# Revit family: Plumbing_Fixture-Grohe-Euroeco_Sequential-32793000-13-METRIC
name_source: partatom
category: Plumbing Fixtures
revit_build: Autodesk Revit 2013 (Build: 20121003_2115(x64)
units: mm (PartAtom-declared; Revit-internal decimal feet)

## types (1)
- Euroeco Special Single
    ADA Compliant = Yes
    Assembly Code = C1030220
    AssetType = Fixed
    Barcode = 0
    CW Connection = Yes
    CWFU = 4.5
    ClassificationName = Uniclass 1.4
    ClassificationValue = L725111
    Cold Water Connection Diameter = 10 mm  [stored 0.0328084 ft]
    Cold Water Radius = 5 mm  [stored 0.0164042 ft]
    Cost = 0 $
    Default Elevation = 600 mm
    Description = Washing your hands with your hands free – this is the idea behind the wall-mounted Euroeco mixers. Wall-mounted installation keeps the basin free, and in order to reduce the risk of accidents caused by projecting parts, faucet levers and spouts are available in a choice of lengths.
    DocumentationCertificates = http://www.grohe.com
    DocumentationInstallationGuide = http://cdn08.grohe.com
    DocumentationLiterature = http://www.grohe.com
    DocumentationMaintenance = http://cdn08.grohe.com
    DocumentationTechnical = http://cdn08.grohe.com
    DurationUnit = Years
    Ecojoy = No
    ExpectedLife = 0
    Flow Pressure = min 0.5 bar/recommended 1 - 5 bar
    Flow Rate = 8 L/min
    HW Connection = Yes
    HWFU = 4.5
    Hot Water Connection Diameter = 10 mm  [stored 0.0328084 ft]
    Hot Water Radius = 5 mm  [stored 0.0164042 ft]
    Keynote = N13
    Low Emitting Material = Yes
    Manufacturer = Grohe AG
    Material = Grohe-Chrome
    Mixing Leaver = Yes
    Model = Euroeco Special Single
    Name = Euroeco Special Single
    Operating Pressure = max 10 bar
    Percentage of Recycled Content = 0
    Product Page URL = http://www.grohe.com
    SerialNumber = 0
    Spare Parts List = http://www.grohe.com
    SpareParts = http://www.grohe.co.uk
    TagNumber = 0
    Temp - Hot Water Supply = max 80°C
    Temp - Hot Water Supply (Recommended) = 60°C
    Test Pressure = 16 bar
    Type Comments = Wash basin mixer wall mounted.
    TypeName = Euroeco Special Single
    URL = www.grohe.com
    Uniclass2 = Pr_40_30_96
    Vent Connection = No
    WFU = 0
    WarrantyDurationUnit = Years
    Waste Connection = No
    _BIMspec_GUID = 0
    _current revision = 1
    _distributed by = www.bimstore.co.uk

note: [stored X ft] marks values corroborated as IEEE doubles in the binary element streams (Revit-internal decimal feet)

## geometry (parser evidence)
native form markers: Blend x6, Sweep x1
no freeform markers — native parametric forms only
